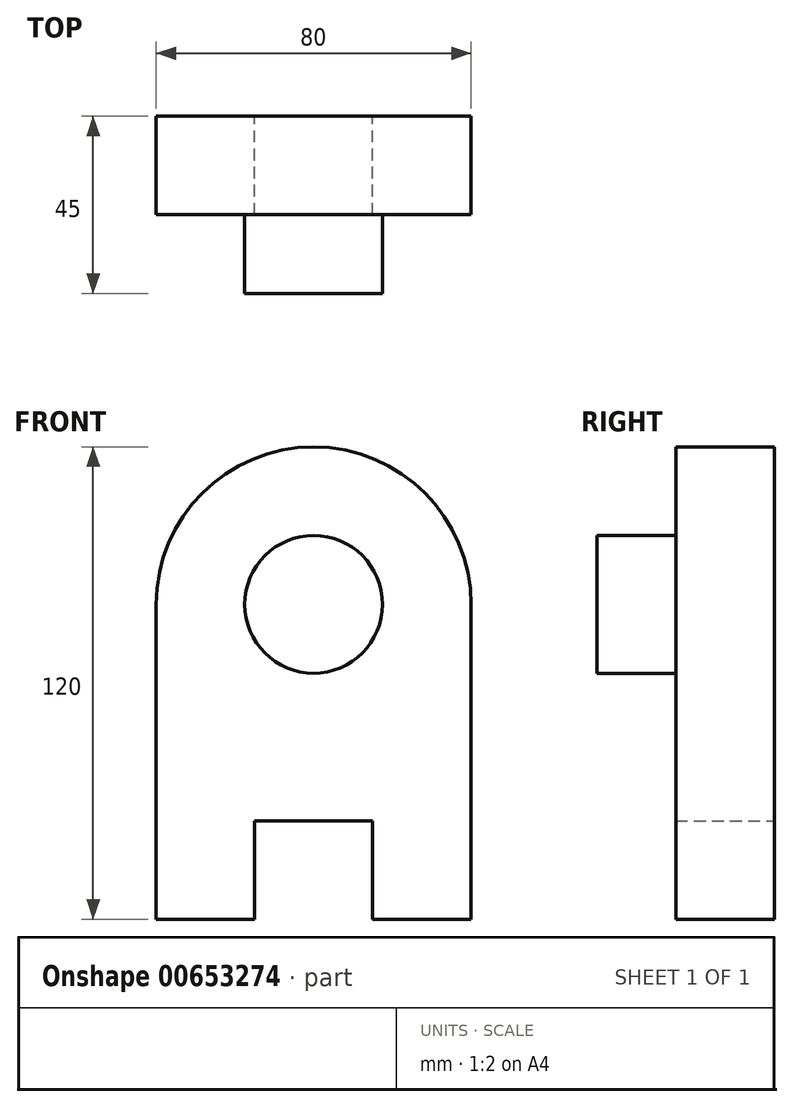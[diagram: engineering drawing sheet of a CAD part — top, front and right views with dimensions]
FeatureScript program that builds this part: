
annotation { "Feature Type Name" : "Feature", "Feature Type Description" : "" }
export const myFeature = defineFeature(function(context is Context, id is Id, definition is map)
    precondition{}
    {
        {
            var Q0;
            Q0=qCreatedBy(makeId("Front.planeOp"),FACE);
            var sketch = newSketch(context, id + "F0", { "sketchPlane" : qUnion([Q0])});
            skLineSegment(sketch, "E0.bottom", {"start": v(40, 40) * mm, "end": v(-40, 40) * mm});
            skLineSegment(sketch, "E0.top", {"start": v(40, -40) * mm, "end": v(15, -40) * mm});
            skLineSegment(sketch, "E0.left", {"start": v(40, 40) * mm, "end": v(40, -40) * mm});
            skLineSegment(sketch, "E0.right", {"start": v(-40, 40) * mm, "end": v(-40, -40) * mm});
            skPoint(sketch, "E0.middle", {"position": v(0, 0) * mm});
            skArc(sketch, "E1", {"start": v(40, 40) * mm, "mid": v(0, 80) * mm, "end": v(-40, 40) * mm});
            skLineSegment(sketch, "E2.top", {"start": v(-15, -15) * mm, "end": v(15, -15) * mm});
            skLineSegment(sketch, "E2.left", {"start": v(-15, -40) * mm, "end": v(-15, -15) * mm});
            skLineSegment(sketch, "E2.right", {"start": v(15, -40) * mm, "end": v(15, -15) * mm});
            skPoint(sketch, "E2.middle", {"position": v(0, -27.5) * mm});
            skLineSegment(sketch, "E3.trimOffspring", {"start": v(-15, -40) * mm, "end": v(-40, -40) * mm});
            skSolve(sketch);
        }
        {
            var Q0;
            Q0=makeQuery(id+"F0.imprint","IMPRINT",FACE,{"disambiguationData":[TD([[makeQuery(id+"F0.imprint","IMPRINT",EDGE,{"derivedFrom":sQuery(id+"F0.wireOp",EDGE,"E0.bottom")}),1.0]])]});
            var Q1;
            Q1=makeQuery(id+"F0.imprint","IMPRINT",FACE,{"disambiguationData":[TD([[makeQuery(id+"F0.imprint","IMPRINT",EDGE,{"derivedFrom":sQuery(id+"F0.wireOp",EDGE,"E0.bottom")}),-1.0]])]});
            extrude(context, id + "F1", {"entities" : qUnion([Q0, Q1]), "depth" : 25 * mm, "offsetDistance" : 25 * mm});
        }
        {
            var Q0;
            Q0=makeQuery(id+"F1.opExtrude","CAP_FACE",FACE,{"disambiguationData":[OSD([sQuery(id+"F0.wireOp",EDGE,"E0.top"),sQuery(id+"F0.wireOp",EDGE,"E0.left"),sQuery(id+"F0.wireOp",EDGE,"E0.right"),sQuery(id+"F0.wireOp",EDGE,"E1"),sQuery(id+"F0.wireOp",EDGE,"E2.top"),sQuery(id+"F0.wireOp",EDGE,"E2.left"),sQuery(id+"F0.wireOp",EDGE,"E2.right"),sQuery(id+"F0.wireOp",EDGE,"E3.trimOffspring")])],"isStart":false});
            var sketch = newSketch(context, id + "F2", { "sketchPlane" : qUnion([Q0])});
            skCircle(sketch, "E4", {"center": v(0, 40) * mm, "radius": 17.5 * mm});
            skSolve(sketch);
        }
        {
            var Q0;
            Q0=makeQuery(id+"F2.imprint","IMPRINT",FACE,{"disambiguationData":[TD([[makeQuery(id+"F2.imprint","IMPRINT",EDGE,{"derivedFrom":sQuery(id+"F2.wireOp",EDGE,"E4")}),1.0]])]});
            extrude(context, id + "F3", {"entities" : qUnion([Q0]), "operationType" : NewBodyOperationType.ADD, "depth" : 20 * mm, "offsetDistance" : 25 * mm});
        }
    });
